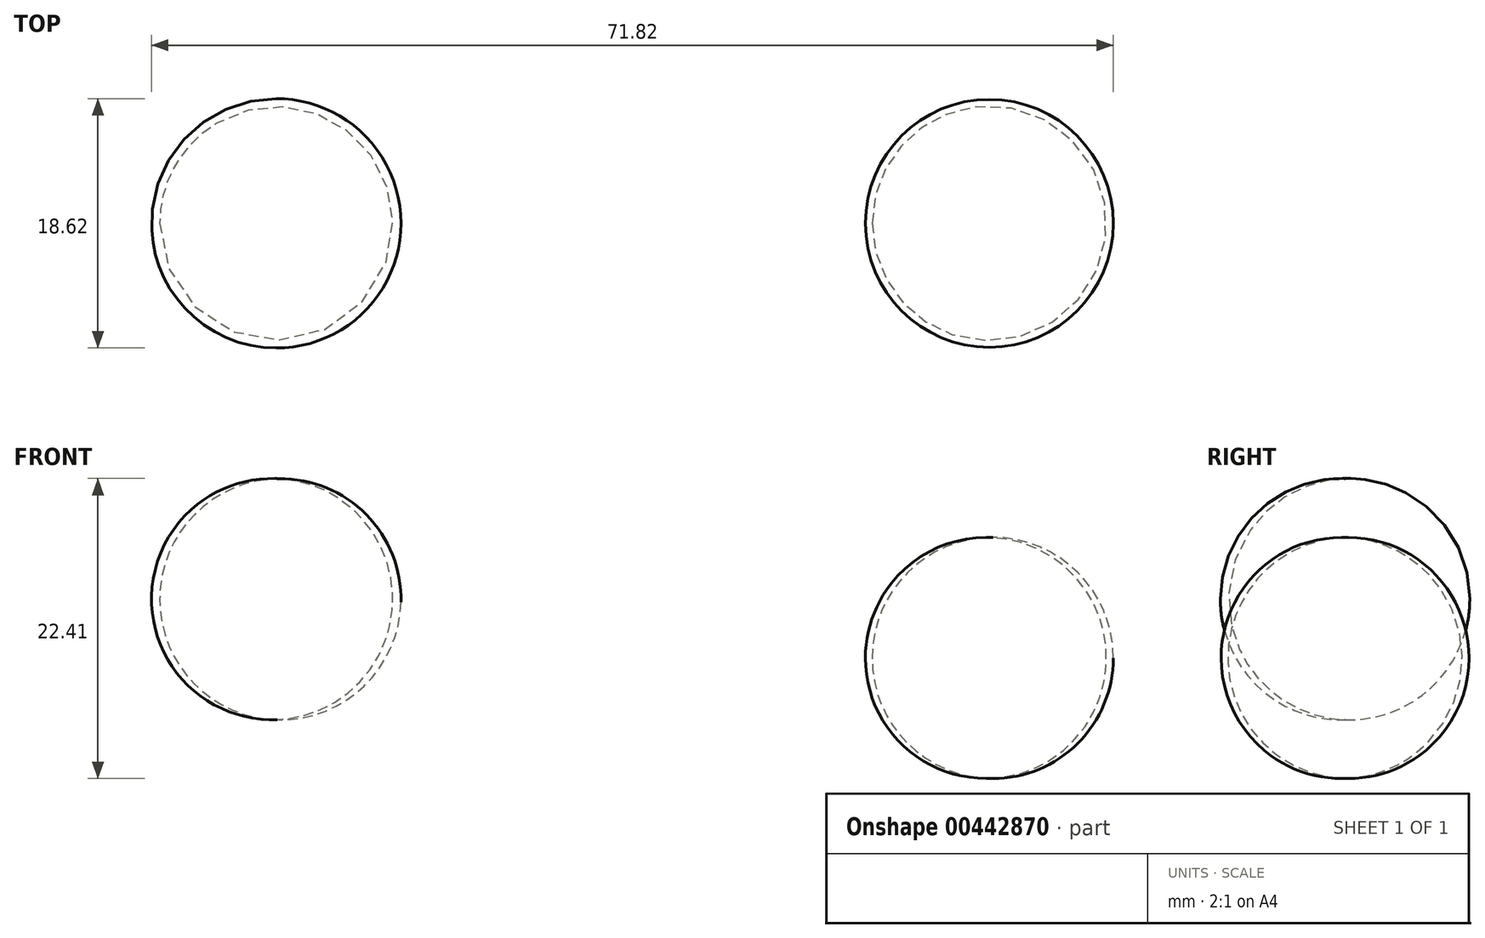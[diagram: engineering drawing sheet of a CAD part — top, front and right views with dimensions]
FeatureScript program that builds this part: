
annotation { "Feature Type Name" : "Feature", "Feature Type Description" : "" }
export const myFeature = defineFeature(function(context is Context, id is Id, definition is map)
    precondition{}
    {
        {
            var Q0;
            Q0=qCreatedBy(makeId("Front.planeOp"),FACE);
            var sketch = newSketch(context, id + "F0", { "sketchPlane" : qUnion([Q0])});
            skArc(sketch, "E0", {"start": v(-24.9, 21.88) * mm, "mid": v(-16, 30.67) * mm, "end": v(-24.48, 39.88) * mm});
            skLineSegment(sketch, "E1", {"start": v(-24.48, 39.88) * mm, "end": v(-24.9, 21.88) * mm});
            skSolve(sketch);
        }
        {
            var Q0;
            Q0 = qSketchRegion(id + "F0", true);
            var Q1;
            Q1=sQuery(id+"F0.wireOp",EDGE,"E1");
            revolve(context, id + "F1", {"entities" : qUnion([Q0]), "axis" : qUnion([Q1]), "revolveType" : RevolveType.FULL});
        }
        {
            var Q0;
            Q0=qCreatedBy(makeId("Front.planeOp"),FACE);
            var sketch = newSketch(context, id + "F2", { "sketchPlane" : qUnion([Q0])});
            skArc(sketch, "E2", {"start": v(28.55, 17.49) * mm, "mid": v(37.81, 26.49) * mm, "end": v(28.55, 35.49) * mm});
            skLineSegment(sketch, "E3", {"start": v(28.55, 35.49) * mm, "end": v(28.55, 17.49) * mm});
            skSolve(sketch);
        }
        {
            var Q0;
            Q0 = qSketchRegion(id + "F2", true);
            var Q1;
            Q1=sQuery(id+"F2.wireOp",EDGE,"E3");
            revolve(context, id + "F3", {"entities" : qUnion([Q0]), "axis" : qUnion([Q1]), "revolveType" : RevolveType.FULL});
        }
    });
